# Revit family: FrameryO-Table.Regular-Seat.Yes-Move.No
name_source: partatom
category: Generic Models
units: mm (PartAtom-declared; Revit-internal decimal feet)

## family parameters
Always vertical = Yes
Can host rebar = No
Cut with Voids When Loaded = No
Part Type = Normal
Room Calculation Point = No
Round Connector Dimension = Use Diameter
Shared = No
Work Plane-Based = No

## types (3) — shared parameters
Back glass width = 10 mm  [stored 0.0328084 ft]
Depth = 1000 mm  [stored 3.28084 ft]
Door material = white RAL 9016 glossy
Door width = 42 mm  [stored 0.137795 ft]
Edges material = Birch plywood
Frame = frame : Exterior Navy
Frame colour = tikkurila ral 620 - 3 misty blue
Front glass width = 11 mm  [stored 0.0360892 ft]
Full colour chart of materials = https://configurator.frameryacoustics.com
Give us feedback = https://www.frameryacoustics.com
Height = 2210 mm  [stored 7.25066 ft]
Internal wall color = Acoustic felt
Laminated sound control glass = Laminated sound control glass
Manufacturer = Framery Oy
Parts material = Brushed stainless steel
Seat color = Framery Wool Light Grey 1000
Seat frame = Brushed stainless steel
Stool = stool : Beige
Table material = white RAL 9016 ultramatt
Width = 1000 mm  [stored 3.28084 ft]
zero-valued in all types: Default Elevation

## per-type parameters (varying)
| type | Exterior | Exterior colour | Regular table | VCR | Void distance | Wide table |
| Framery O Standard wide table | Exterior : Exterior Misty Blue | Black Grey NCS S 8500-N | No | No | 390 mm  [stored 1.27953 ft] | Yes |
| Framery O VCR | Exterior : Exterior Winter Moss | white RAL 9016 glossy | No | Yes | 437 mm  [stored 1.43373 ft] | No |
| Framery O Standard regular table - White | Exterior : Exterior Misty Blue | white RAL 9016 glossy | Yes | No | 390 mm  [stored 1.27953 ft] | No |

note: [stored X ft] marks values corroborated as IEEE doubles in the binary element streams (Revit-internal decimal feet)

## geometry (parser evidence)
native form markers: Sweep x68
no freeform markers — native parametric forms only
